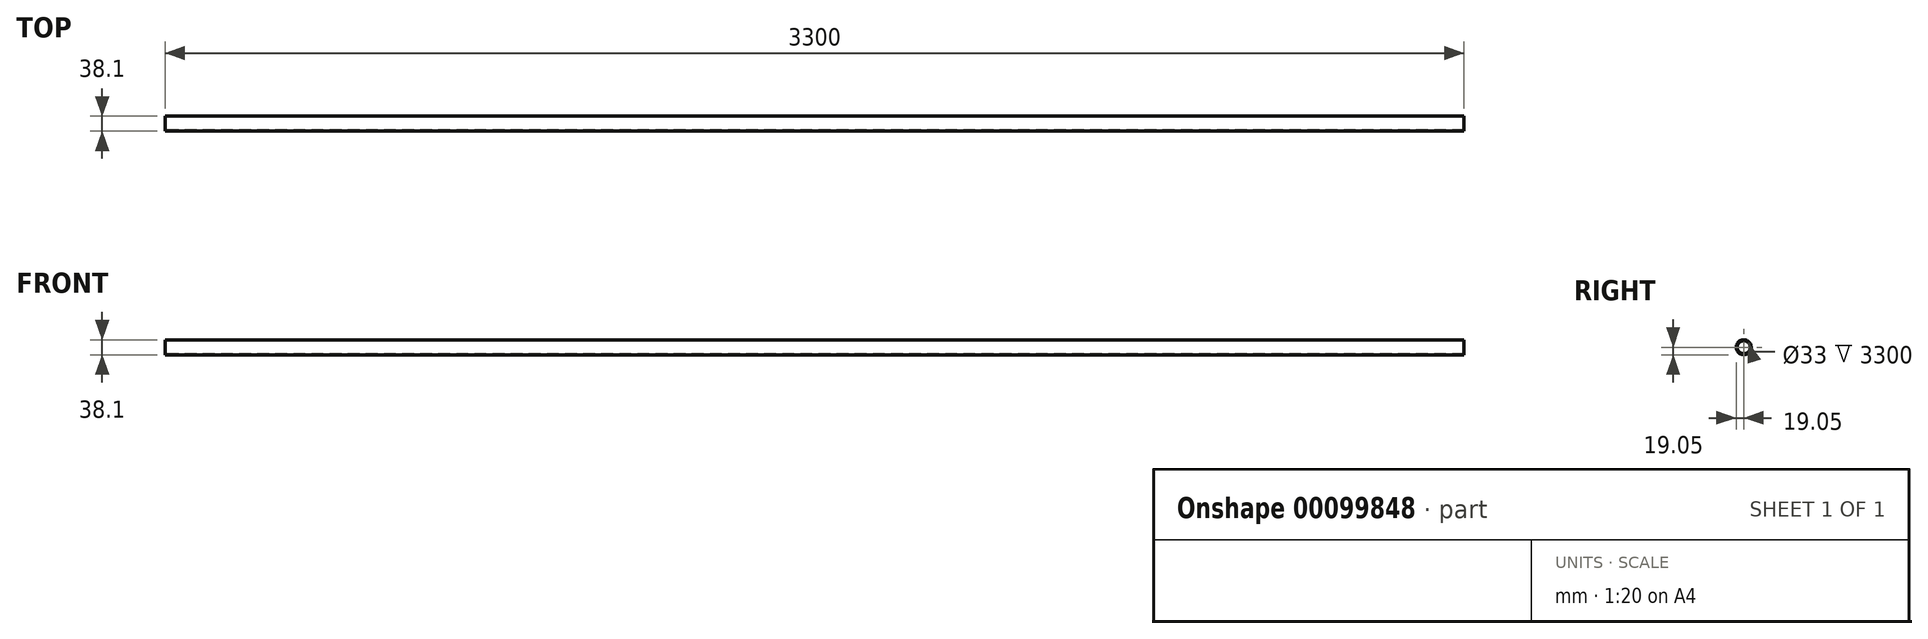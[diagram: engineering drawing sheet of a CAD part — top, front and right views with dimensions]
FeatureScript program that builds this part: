
annotation { "Feature Type Name" : "Feature", "Feature Type Description" : "" }
export const myFeature = defineFeature(function(context is Context, id is Id, definition is map)
    precondition{}
    {
        {
            var Q0;
            Q0=qCreatedBy(makeId("Right.planeOp"),FACE);
            var sketch = newSketch(context, id + "F0", { "sketchPlane" : qUnion([Q0])});
            skCircle(sketch, "E0", {"center": v(0, 0) * mm, "radius": 19.05 * mm});
            skCircle(sketch, "E1", {"center": v(0, 0) * mm, "radius": 16.5 * mm});
            skSolve(sketch);
        }
        {
            var Q0;
            Q0 = qSketchRegion(id + "F0", true);
            extrude(context, id + "F1", {"entities" : qUnion([Q0]), "endBound" : BoundingType.SYMMETRIC, "depth" : 3300 * mm});
        }
    });
